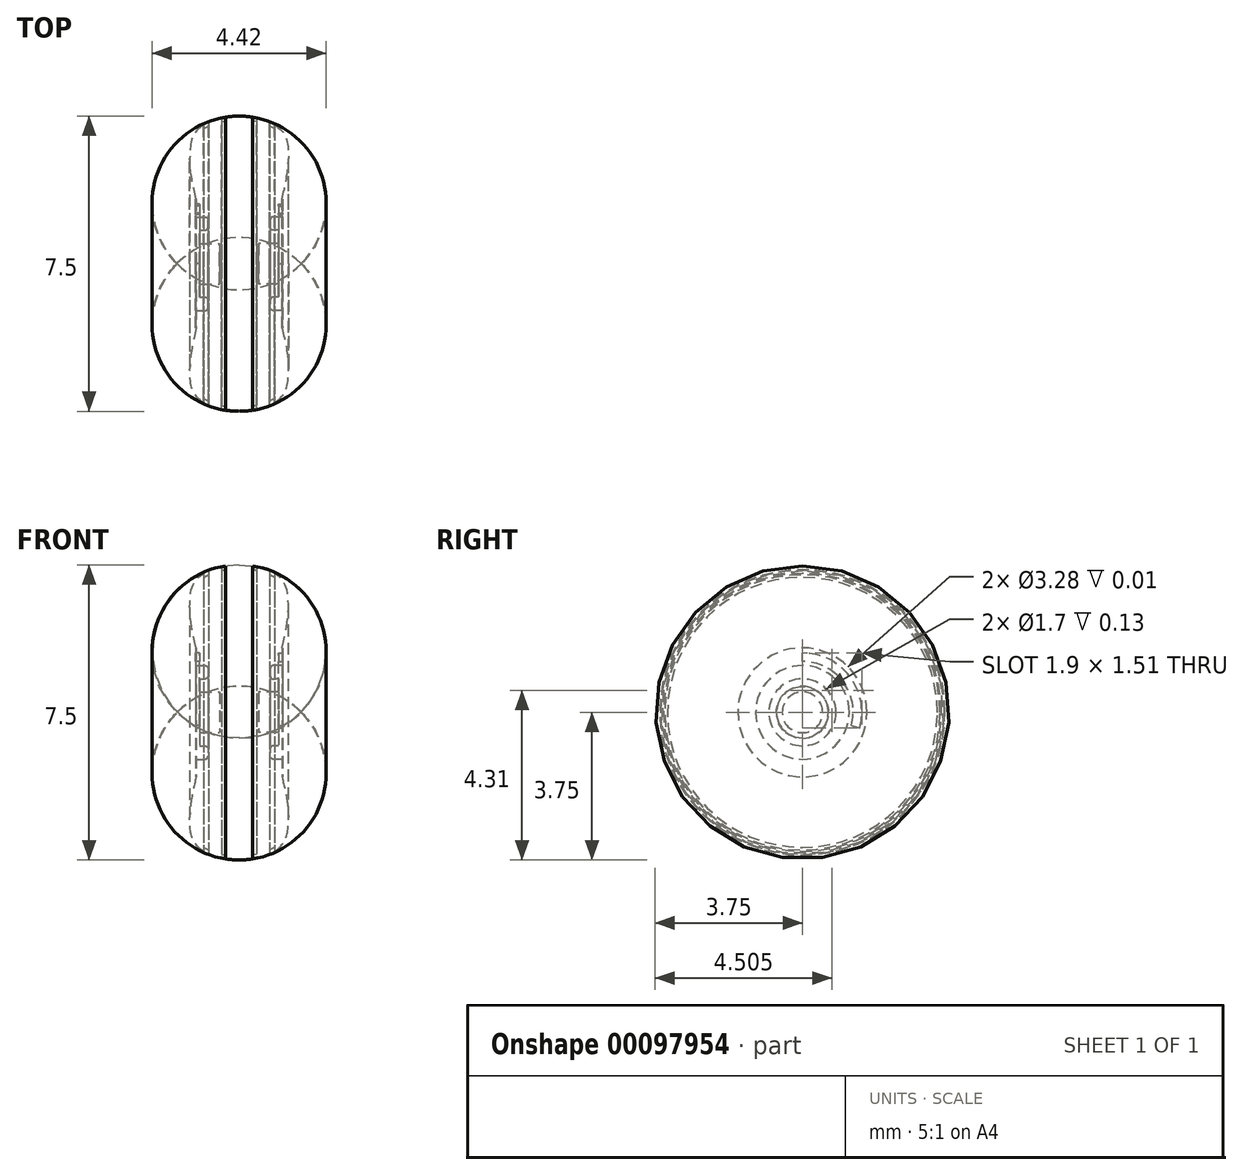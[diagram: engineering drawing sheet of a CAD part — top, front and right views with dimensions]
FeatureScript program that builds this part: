
annotation { "Feature Type Name" : "Feature", "Feature Type Description" : "" }
export const myFeature = defineFeature(function(context is Context, id is Id, definition is map)
    precondition{}
    {
        {
            var Q0;
            Q0=qCreatedBy(makeId("Front.planeOp"),FACE);
            var sketch = newSketch(context, id + "F0", { "sketchPlane" : qUnion([Q0])});
            skLineSegment(sketch, "E0.top", {"start": v(0.87, 0.85) * mm, "end": v(1, 0.85) * mm});
            skLineSegment(sketch, "E0.right", {"start": v(1, 0.51) * mm, "end": v(1, 0.85) * mm});
            skLineSegment(sketch, "E1", {"start": v(0.8, 0.93) * mm, "end": v(0.8, 1.1) * mm});
            skLineSegment(sketch, "E2", {"start": v(0.87, 1.19) * mm, "end": v(1.1, 1.19) * mm});
            skLineSegment(sketch, "E3", {"start": v(1.1, 1.59) * mm, "end": v(1.1, 1.64) * mm});
            skLineSegment(sketch, "E4", {"start": v(1.12, 1.64) * mm, "end": v(1.09, 1.64) * mm});
            skPoint(sketch, "E5.orphan", {"position": v(0, 1.19) * mm});
            skPoint(sketch, "E6.visualSharp", {"position": v(1.1, 1.19) * mm});
            skPoint(sketch, "E7.visualSharp", {"position": v(0.8, 1.19) * mm});
            skArc(sketch, "E7.filletArc", {"start": v(0.87, 1.19) * mm, "mid": v(0.81, 1.17) * mm, "end": v(0.8, 1.1) * mm});
            skArc(sketch, "E8.filletArc", {"start": v(0.8, 0.93) * mm, "mid": v(0.81, 0.87) * mm, "end": v(0.87, 0.85) * mm});
            skPoint(sketch, "E9.visualSharp", {"position": v(1.17, 1.64) * mm});
            skArc(sketch, "E9.filletArc", {"start": v(1.17, 1.59) * mm, "mid": v(1.16, 1.63) * mm, "end": v(1.12, 1.64) * mm});
            skLineSegment(sketch, "E10", {"start": v(-0.76, 3.75) * mm, "end": v(0, 3.75) * mm, "construction": true});
            skLineSegment(sketch, "E11", {"start": v(1.25, 3.84) * mm, "end": v(1.25, 0.98) * mm, "construction": true});
            skLineSegment(sketch, "E12", {"start": v(0, 3.75) * mm, "end": v(1.72, 3.75) * mm, "construction": true});
            skLineSegment(sketch, "E13", {"start": v(1.17, 1.59) * mm, "end": v(1.1, 1.59) * mm});
            skLineSegment(sketch, "E14", {"start": v(1.25, 1.19) * mm, "end": v(1.27, 1.19) * mm});
            skLineSegment(sketch, "E15", {"start": v(1.1, 1.19) * mm, "end": v(1.1, 1.64) * mm});
            skPoint(sketch, "E16.orphan", {"position": v(0, 0.73) * mm});
            skLineSegment(sketch, "E17", {"start": v(0, 0.73) * mm, "end": v(0, 5.2) * mm, "construction": true});
            skLineSegment(sketch, "E18", {"start": v(0.5, 0.52) * mm, "end": v(1, 0.52) * mm});
            skLineSegment(sketch, "E19", {"start": v(0.57, 0) * mm, "end": v(0.57, -0.77) * mm, "construction": true});
            skLineSegment(sketch, "E20", {"start": v(1.1, 4.64) * mm, "end": v(1.1, 3.06) * mm, "construction": true});
            skLineSegment(sketch, "E21", {"start": v(0.97, 3.34) * mm, "end": v(1.1, 3.34) * mm, "construction": true});
            skFitSpline(sketch, "E22", {"points": [v(1.09, 1.64) * mm, v(1.25, 2.8) * mm, v(1.1, 3.34) * mm, v(0, 3.75) * mm], "startDerivative": vector(1.3, 5.18) * mm, "endDerivative": vector(-4.24, 0) * mm});
            skPoint(sketch, "E23", {"position": v(1.25, 2.41) * mm});
            skLineSegment(sketch, "E24", {"start": v(0.34, 3.93) * mm, "end": v(0.34, 3.62) * mm, "construction": true});
            skLineSegment(sketch, "E25", {"start": v(0.44, 3.93) * mm, "end": v(0.44, 3.6) * mm, "construction": true});
            skLineSegment(sketch, "E26", {"start": v(0.78, 3.93) * mm, "end": v(0.78, 3.5) * mm, "construction": true});
            skLineSegment(sketch, "E27", {"start": v(0.9, 3.95) * mm, "end": v(0.9, 3.43) * mm, "construction": true});
            skLineSegment(sketch, "E28", {"start": v(0.34, 3.62) * mm, "end": v(0.44, 3.6) * mm});
            skLineSegment(sketch, "E29", {"start": v(0.78, 3.5) * mm, "end": v(0.9, 3.43) * mm});
            skLineSegment(sketch, "E30", {"start": v(0.34, 3.72) * mm, "end": v(0.34, 3.62) * mm});
            skLineSegment(sketch, "E31", {"start": v(0.44, 3.6) * mm, "end": v(0.44, 3.7) * mm});
            skLineSegment(sketch, "E32", {"start": v(0.78, 3.5) * mm, "end": v(0.78, 3.6) * mm});
            skLineSegment(sketch, "E33", {"start": v(0.9, 3.43) * mm, "end": v(0.9, 3.53) * mm});
            skLineSegment(sketch, "E34", {"start": v(0, 0.52) * mm, "end": v(0, 3.75) * mm});
            skLineSegment(sketch, "E35", {"start": v(0, 0.52) * mm, "end": v(0, 0) * mm});
            skLineSegment(sketch, "E36", {"start": v(0.5, 0) * mm, "end": v(0.5, 0.52) * mm});
            skLineSegment(sketch, "E37", {"start": v(0, 0) * mm, "end": v(0.5, 0) * mm});
            skSolve(sketch);
        }
        {
            var Q0;
            Q0=makeQuery(id+"F0.imprint","IMPRINT",FACE,{"disambiguationData":[TD([[makeQuery(id+"F0.imprint","IMPRINT",EDGE,{"derivedFrom":sQuery(id+"F0.wireOp",EDGE,"E0.top")}),-1.0]])]});
            var Q1;
            Q1=sQuery(id+"F0.wireOp",EDGE,"8bb111fc-4642-4fca-a44e-8b574824e9490.MirrorCS");
            var Q2;
            Q2=sQuery(id+"F0.wireOp",EDGE,"5d76dffb-9663-4801-85ba-127905f750e50.MirrorCS");
            var Q3;
            Q3=sQuery(id+"F0.wireOp",EDGE,"d13460d5-a523-4224-9297-77c6a2cba0c50.MirrorCS");
            var Q4;
            Q4=sQuery(id+"F0.wireOp",EDGE,"c0737af9-8dda-4185-ab45-cae04200aa6d0.MirrorCS");
            var Q5;
            Q5=sQuery(id+"F0.wireOp",EDGE,"E37");
            revolve(context, id + "F1", {"entities" : qUnion([Q0]), "surfaceEntities" : qUnion([Q1, Q2, Q3, Q4]), "axis" : qUnion([Q5]), "revolveType" : RevolveType.FULL});
        }
        {
            var Q0;
            Q0=qCreatedBy(makeId("Front.planeOp"),FACE);
            var sketch = newSketch(context, id + "F2", { "sketchPlane" : qUnion([Q0])});
            skLineSegment(sketch, "E38.bottom", {"start": v(1, 1.51) * mm, "end": v(1.2, 1.51) * mm});
            skLineSegment(sketch, "E38.top", {"start": v(1, 1.29) * mm, "end": v(1.2, 1.29) * mm});
            skLineSegment(sketch, "E38.left", {"start": v(1, 1.51) * mm, "end": v(1, 1.29) * mm});
            skLineSegment(sketch, "E38.right", {"start": v(1.2, 1.51) * mm, "end": v(1.2, 1.29) * mm});
            skLineSegment(sketch, "E39", {"start": v(0, 0) * mm, "end": v(2.72, 0) * mm, "construction": true});
            skSolve(sketch);
        }
        {
            var Q0;
            Q0=qSketchRegion(id+"F2",true);
            var Q1;
            Q1=sQuery(id+"F2.wireOp",EDGE,"E39");
            revolve(context, id + "F3", {"operationType" : NewBodyOperationType.REMOVE, "entities" : qUnion([Q0]), "axis" : qUnion([Q1]), "revolveType" : RevolveType.ONE_DIRECTION, "oppositeDirection" : true, "angle" : 105 * degree});
        }
        {
            var Q0;
            Q0=makeQuery(id+"F1.opRevolve","SWEPT_BODY",BODY,{"disambiguationData":[OSD([sQuery(id+"F0.wireOp",EDGE,"E0.top"),sQuery(id+"F0.wireOp",EDGE,"E0.right"),sQuery(id+"F0.wireOp",EDGE,"E1"),sQuery(id+"F0.wireOp",EDGE,"E2"),sQuery(id+"F0.wireOp",EDGE,"E4"),sQuery(id+"F0.wireOp",EDGE,"E7.filletArc"),sQuery(id+"F0.wireOp",EDGE,"E8.filletArc"),sQuery(id+"F0.wireOp",EDGE,"E15"),sQuery(id+"F0.wireOp",EDGE,"E18"),sQuery(id+"F0.wireOp",EDGE,"E22"),sQuery(id+"F0.wireOp",EDGE,"E28"),sQuery(id+"F0.wireOp",EDGE,"E29"),sQuery(id+"F0.wireOp",EDGE,"E30"),sQuery(id+"F0.wireOp",EDGE,"E31"),sQuery(id+"F0.wireOp",EDGE,"E32"),sQuery(id+"F0.wireOp",EDGE,"E33"),sQuery(id+"F0.wireOp",EDGE,"E22"),sQuery(id+"F0.wireOp",EDGE,"E22"),sQuery(id+"F0.wireOp",EDGE,"E34")])]});
            var Q1;
            Q1=makeQuery(id+"F1.opRevolve","SWEPT_FACE",FACE,{"disambiguationData":[OSD([sQuery(id+"F0.wireOp",EDGE,"E34")])]});
            mirror(context, id + "F4", {"operationType" : NewBodyOperationType.ADD, "entities" : qUnion([Q0]), "mirrorPlane" : qUnion([Q1])});
        }
    });
